# Revit family: Haworth_HC1Pedestal_Cushion_EU_PRELIMINARY
name_source: partatom
category: Furniture Systems
units: mm (PartAtom-declared; Revit-internal decimal feet)

## family parameters
Always vertical = Yes
Cut with Voids When Loaded = No
OmniClass Number = 23.40.70.14.64.21
OmniClass Title = Systems Furniture
Part Type = Normal
Room Calculation Point = No
Round Connector Dimension = Use Diameter
Shared = No
Work Plane-Based = No

## types (4) — shared parameters
Actual Depth = 43 cm
Assembly Code = E2020200
Description = Haworth - HC1 Pedestal - Pedestal Cushion
Manufacturer = Haworth
Model = D9551XXX
Revision Number = 1
Size = Verify Final Dim. w/ Haworth
URL = https://www.haworth.com
URL - Product = https://www.haworth.com
Warranty = http://www.haworth.com

## per-type parameters (varying)
| type | Actual Width | High | Large | Low | Small | Thickness |
| 43 x 60 x 6 | 60 cm | Yes | No | No | Yes | 6 cm |
| 43 x 80 x 6 | 80 cm | Yes | Yes | No | No | 6 cm |
| 43 x 80 x 4 | 80 cm | No | Yes | Yes | No | 4 cm |
| 43 x 60 x 4 | 60 cm | No | No | Yes | Yes | 4 cm |

## geometry (parser evidence)
native form markers: Sweep x2
no freeform markers — native parametric forms only
